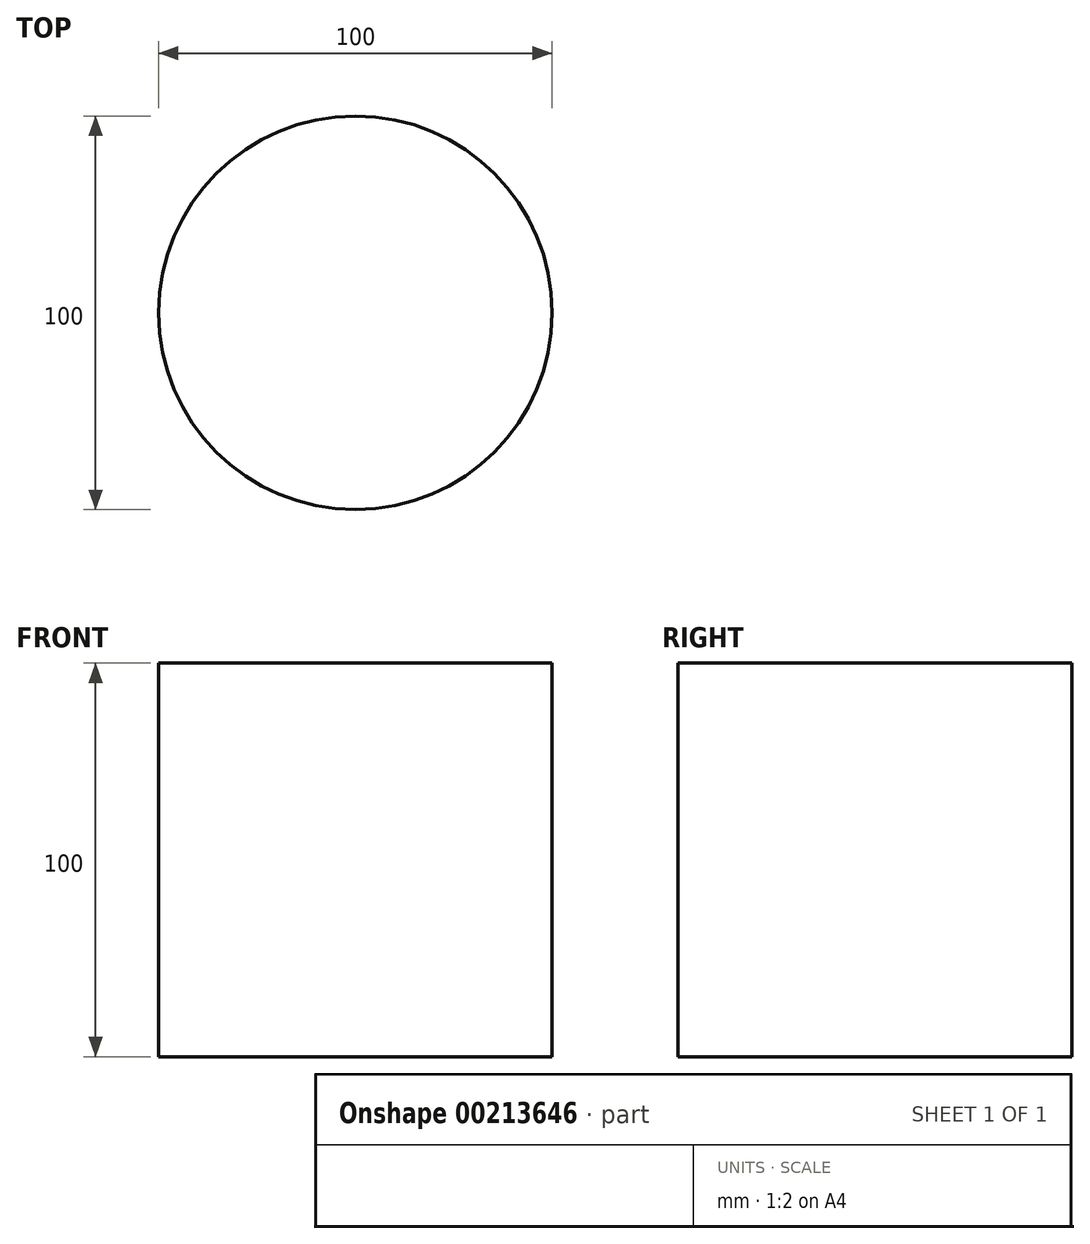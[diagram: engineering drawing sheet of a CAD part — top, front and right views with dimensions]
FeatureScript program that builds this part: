
annotation { "Feature Type Name" : "Feature", "Feature Type Description" : "" }
export const myFeature = defineFeature(function(context is Context, id is Id, definition is map)
    precondition{}
    {
        {
            var Q0;
            Q0=qCreatedBy(makeId("Top.planeOp"),FACE);
            var sketch = newSketch(context, id + "F0", { "sketchPlane" : qUnion([Q0])});
            skCircle(sketch, "E0", {"center": v(0, 0) * mm, "radius": 50 * mm});
            skSolve(sketch);
        }
        {
            var Q0;
            Q0=makeQuery(id+"F0.imprint","IMPRINT",FACE,{"disambiguationData":[TD([[makeQuery(id+"F0.imprint","IMPRINT",EDGE,{"derivedFrom":sQuery(id+"F0.wireOp",EDGE,"E0")}),1.0]])]});
            extrude(context, id + "F1", {"entities" : qUnion([Q0]), "depth" : 100 * mm});
        }
    });
